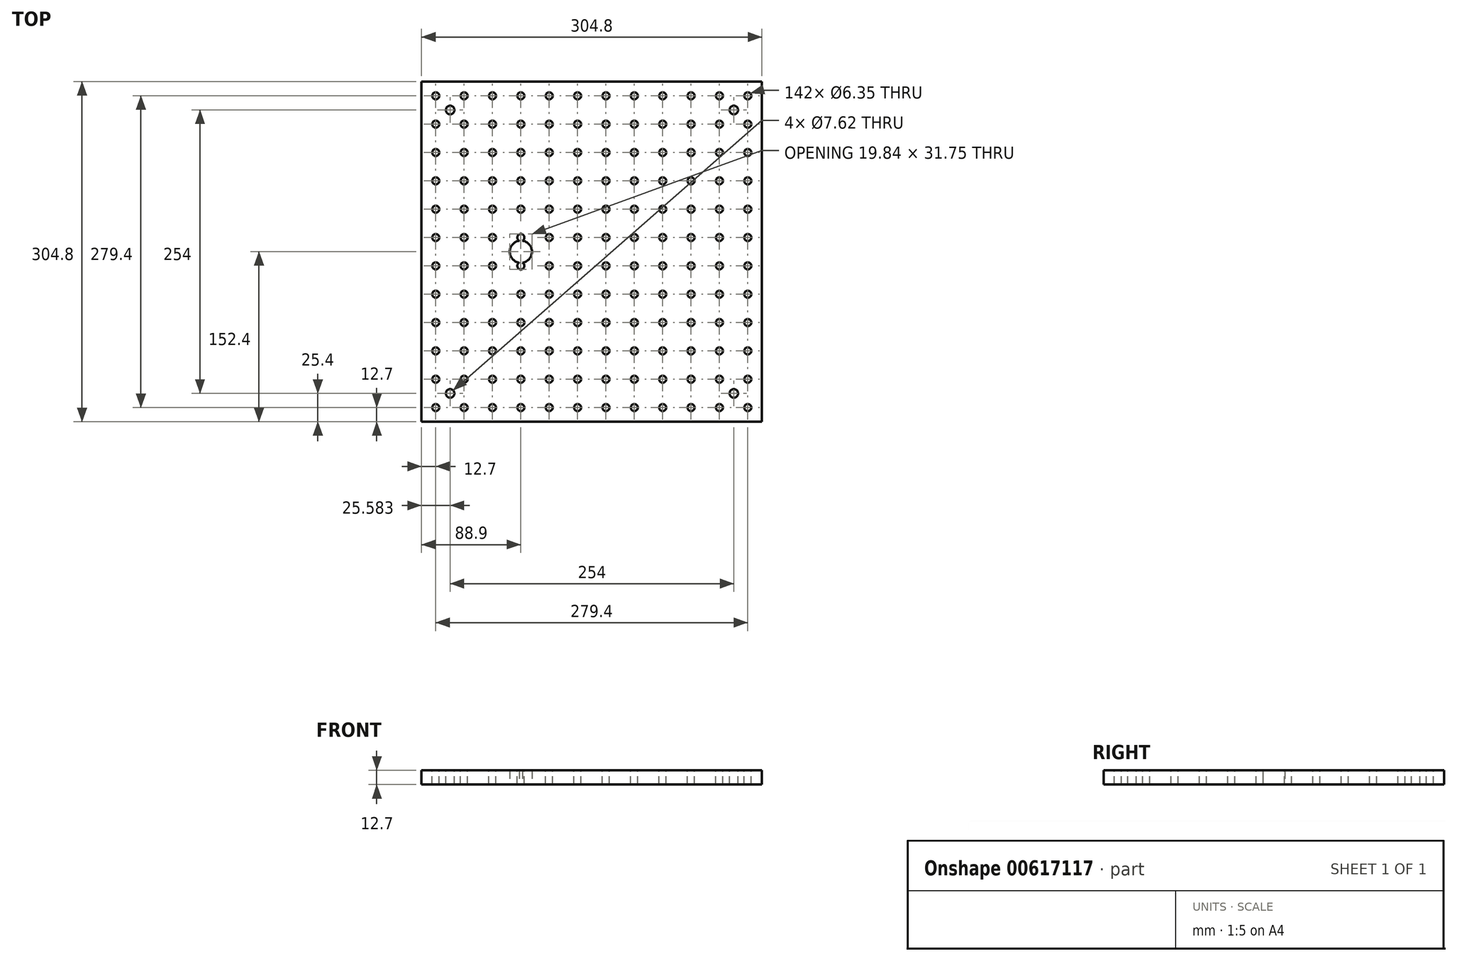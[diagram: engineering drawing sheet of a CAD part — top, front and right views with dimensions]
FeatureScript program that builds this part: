
annotation { "Feature Type Name" : "Feature", "Feature Type Description" : "" }
export const myFeature = defineFeature(function(context is Context, id is Id, definition is map)
    precondition{}
    {
        {
            var Q0;
            Q0=qCreatedBy(makeId("Top.planeOp"),FACE);
            var sketch = newSketch(context, id + "F0", { "sketchPlane" : qUnion([Q0])});
            skLineSegment(sketch, "E0.bottom", {"start": v(-152.4, 152.4) * mm, "end": v(152.4, 152.4) * mm});
            skLineSegment(sketch, "E0.top", {"start": v(-152.4, -152.4) * mm, "end": v(152.4, -152.4) * mm});
            skLineSegment(sketch, "E0.left", {"start": v(-152.4, 152.4) * mm, "end": v(-152.4, -152.4) * mm});
            skLineSegment(sketch, "E0.right", {"start": v(152.4, 152.4) * mm, "end": v(152.4, -152.4) * mm});
            skSolve(sketch);
        }
        {
            var Q0;
            Q0=qSketchRegion(id+"F0",true);
            extrude(context, id + "F1", {"entities" : qUnion([Q0]), "depth" : 12.7 * mm, "offsetDistance" : 25.4 * mm});
        }
        {
            var Q0;
            Q0=makeQuery(id+"F1.opExtrude","CAP_FACE",FACE,{"disambiguationData":[OSD([sQuery(id+"F0.wireOp",EDGE,"E0.bottom"),sQuery(id+"F0.wireOp",EDGE,"E0.top"),sQuery(id+"F0.wireOp",EDGE,"E0.left"),sQuery(id+"F0.wireOp",EDGE,"E0.right")])],"isStart":false});
            var sketch = newSketch(context, id + "F2", { "sketchPlane" : qUnion([Q0])});
            skCircle(sketch, "E1", {"center": v(-139.7, -139.7) * mm, "radius": 3.18 * mm});
            skCircle(sketch, "E2.0.1.0", {"center": v(-139.7, -114.3) * mm, "radius": 3.18 * mm});
            skCircle(sketch, "E2.0.2.0", {"center": v(-139.7, -88.9) * mm, "radius": 3.18 * mm});
            skCircle(sketch, "E2.0.3.0", {"center": v(-139.7, -63.5) * mm, "radius": 3.18 * mm});
            skCircle(sketch, "E2.0.4.0", {"center": v(-139.7, -38.1) * mm, "radius": 3.18 * mm});
            skCircle(sketch, "E2.0.5.0", {"center": v(-139.7, -12.7) * mm, "radius": 3.18 * mm});
            skCircle(sketch, "E2.0.6.0", {"center": v(-139.7, 12.7) * mm, "radius": 3.18 * mm});
            skCircle(sketch, "E2.0.7.0", {"center": v(-139.7, 38.1) * mm, "radius": 3.18 * mm});
            skCircle(sketch, "E2.0.8.0", {"center": v(-139.7, 63.5) * mm, "radius": 3.18 * mm});
            skCircle(sketch, "E2.0.9.0", {"center": v(-139.7, 88.9) * mm, "radius": 3.18 * mm});
            skCircle(sketch, "E2.0.10.0", {"center": v(-139.7, 114.3) * mm, "radius": 3.18 * mm});
            skCircle(sketch, "E2.1.0.0", {"center": v(-114.3, -139.7) * mm, "radius": 3.18 * mm});
            skCircle(sketch, "E2.1.1.0", {"center": v(-114.3, -114.3) * mm, "radius": 3.18 * mm});
            skCircle(sketch, "E2.1.2.0", {"center": v(-114.3, -88.9) * mm, "radius": 3.18 * mm});
            skCircle(sketch, "E2.1.3.0", {"center": v(-114.3, -63.5) * mm, "radius": 3.18 * mm});
            skCircle(sketch, "E2.1.4.0", {"center": v(-114.3, -38.1) * mm, "radius": 3.18 * mm});
            skCircle(sketch, "E2.1.5.0", {"center": v(-114.3, -12.7) * mm, "radius": 3.18 * mm});
            skCircle(sketch, "E2.1.6.0", {"center": v(-114.3, 12.7) * mm, "radius": 3.18 * mm});
            skCircle(sketch, "E2.1.7.0", {"center": v(-114.3, 38.1) * mm, "radius": 3.18 * mm});
            skCircle(sketch, "E2.1.8.0", {"center": v(-114.3, 63.5) * mm, "radius": 3.18 * mm});
            skCircle(sketch, "E2.1.9.0", {"center": v(-114.3, 88.9) * mm, "radius": 3.18 * mm});
            skCircle(sketch, "E2.1.10.0", {"center": v(-114.3, 114.3) * mm, "radius": 3.18 * mm});
            skCircle(sketch, "E2.2.0.0", {"center": v(-88.9, -139.7) * mm, "radius": 3.18 * mm});
            skCircle(sketch, "E2.2.1.0", {"center": v(-88.9, -114.3) * mm, "radius": 3.18 * mm});
            skCircle(sketch, "E2.2.2.0", {"center": v(-88.9, -88.9) * mm, "radius": 3.18 * mm});
            skCircle(sketch, "E2.2.3.0", {"center": v(-88.9, -63.5) * mm, "radius": 3.18 * mm});
            skCircle(sketch, "E2.2.4.0", {"center": v(-88.9, -38.1) * mm, "radius": 3.18 * mm});
            skCircle(sketch, "E2.2.5.0", {"center": v(-88.9, -12.7) * mm, "radius": 3.18 * mm});
            skCircle(sketch, "E2.2.6.0", {"center": v(-88.9, 12.7) * mm, "radius": 3.18 * mm});
            skCircle(sketch, "E2.2.7.0", {"center": v(-88.9, 38.1) * mm, "radius": 3.18 * mm});
            skCircle(sketch, "E2.2.8.0", {"center": v(-88.9, 63.5) * mm, "radius": 3.18 * mm});
            skCircle(sketch, "E2.2.9.0", {"center": v(-88.9, 88.9) * mm, "radius": 3.18 * mm});
            skCircle(sketch, "E2.2.10.0", {"center": v(-88.9, 114.3) * mm, "radius": 3.18 * mm});
            skCircle(sketch, "E2.3.0.0", {"center": v(-63.5, -139.7) * mm, "radius": 3.18 * mm});
            skCircle(sketch, "E2.3.1.0", {"center": v(-63.5, -114.3) * mm, "radius": 3.18 * mm});
            skCircle(sketch, "E2.3.2.0", {"center": v(-63.5, -88.9) * mm, "radius": 3.18 * mm});
            skCircle(sketch, "E2.3.3.0", {"center": v(-63.5, -63.5) * mm, "radius": 3.18 * mm});
            skCircle(sketch, "E2.3.4.0", {"center": v(-63.5, -38.1) * mm, "radius": 3.18 * mm});
            skCircle(sketch, "E2.3.5.0", {"center": v(-63.5, -12.7) * mm, "radius": 3.18 * mm});
            skCircle(sketch, "E2.3.6.0", {"center": v(-63.5, 12.7) * mm, "radius": 3.18 * mm});
            skCircle(sketch, "E2.3.7.0", {"center": v(-63.5, 38.1) * mm, "radius": 3.18 * mm});
            skCircle(sketch, "E2.3.8.0", {"center": v(-63.5, 63.5) * mm, "radius": 3.18 * mm});
            skCircle(sketch, "E2.3.9.0", {"center": v(-63.5, 88.9) * mm, "radius": 3.18 * mm});
            skCircle(sketch, "E2.3.10.0", {"center": v(-63.5, 114.3) * mm, "radius": 3.18 * mm});
            skCircle(sketch, "E2.4.0.0", {"center": v(-38.1, -139.7) * mm, "radius": 3.18 * mm});
            skCircle(sketch, "E2.4.1.0", {"center": v(-38.1, -114.3) * mm, "radius": 3.18 * mm});
            skCircle(sketch, "E2.4.2.0", {"center": v(-38.1, -88.9) * mm, "radius": 3.18 * mm});
            skCircle(sketch, "E2.4.3.0", {"center": v(-38.1, -63.5) * mm, "radius": 3.18 * mm});
            skCircle(sketch, "E2.4.4.0", {"center": v(-38.1, -38.1) * mm, "radius": 3.18 * mm});
            skCircle(sketch, "E2.4.5.0", {"center": v(-38.1, -12.7) * mm, "radius": 3.18 * mm});
            skCircle(sketch, "E2.4.6.0", {"center": v(-38.1, 12.7) * mm, "radius": 3.18 * mm});
            skCircle(sketch, "E2.4.7.0", {"center": v(-38.1, 38.1) * mm, "radius": 3.18 * mm});
            skCircle(sketch, "E2.4.8.0", {"center": v(-38.1, 63.5) * mm, "radius": 3.18 * mm});
            skCircle(sketch, "E2.4.9.0", {"center": v(-38.1, 88.9) * mm, "radius": 3.18 * mm});
            skCircle(sketch, "E2.4.10.0", {"center": v(-38.1, 114.3) * mm, "radius": 3.18 * mm});
            skCircle(sketch, "E2.5.0.0", {"center": v(-12.7, -139.7) * mm, "radius": 3.18 * mm});
            skCircle(sketch, "E2.5.1.0", {"center": v(-12.7, -114.3) * mm, "radius": 3.18 * mm});
            skCircle(sketch, "E2.5.2.0", {"center": v(-12.7, -88.9) * mm, "radius": 3.18 * mm});
            skCircle(sketch, "E2.5.3.0", {"center": v(-12.7, -63.5) * mm, "radius": 3.18 * mm});
            skCircle(sketch, "E2.5.4.0", {"center": v(-12.7, -38.1) * mm, "radius": 3.18 * mm});
            skCircle(sketch, "E2.5.5.0", {"center": v(-12.7, -12.7) * mm, "radius": 3.18 * mm});
            skCircle(sketch, "E2.5.6.0", {"center": v(-12.7, 12.7) * mm, "radius": 3.18 * mm});
            skCircle(sketch, "E2.5.7.0", {"center": v(-12.7, 38.1) * mm, "radius": 3.18 * mm});
            skCircle(sketch, "E2.5.8.0", {"center": v(-12.7, 63.5) * mm, "radius": 3.18 * mm});
            skCircle(sketch, "E2.5.9.0", {"center": v(-12.7, 88.9) * mm, "radius": 3.18 * mm});
            skCircle(sketch, "E2.5.10.0", {"center": v(-12.7, 114.3) * mm, "radius": 3.18 * mm});
            skCircle(sketch, "E2.6.0.0", {"center": v(12.7, -139.7) * mm, "radius": 3.18 * mm});
            skCircle(sketch, "E2.6.1.0", {"center": v(12.7, -114.3) * mm, "radius": 3.18 * mm});
            skCircle(sketch, "E2.6.2.0", {"center": v(12.7, -88.9) * mm, "radius": 3.18 * mm});
            skCircle(sketch, "E2.6.3.0", {"center": v(12.7, -63.5) * mm, "radius": 3.18 * mm});
            skCircle(sketch, "E2.6.4.0", {"center": v(12.7, -38.1) * mm, "radius": 3.18 * mm});
            skCircle(sketch, "E2.6.5.0", {"center": v(12.7, -12.7) * mm, "radius": 3.18 * mm});
            skCircle(sketch, "E2.6.6.0", {"center": v(12.7, 12.7) * mm, "radius": 3.18 * mm});
            skCircle(sketch, "E2.6.7.0", {"center": v(12.7, 38.1) * mm, "radius": 3.18 * mm});
            skCircle(sketch, "E2.6.8.0", {"center": v(12.7, 63.5) * mm, "radius": 3.18 * mm});
            skCircle(sketch, "E2.6.9.0", {"center": v(12.7, 88.9) * mm, "radius": 3.18 * mm});
            skCircle(sketch, "E2.6.10.0", {"center": v(12.7, 114.3) * mm, "radius": 3.18 * mm});
            skCircle(sketch, "E2.7.0.0", {"center": v(38.1, -139.7) * mm, "radius": 3.18 * mm});
            skCircle(sketch, "E2.7.1.0", {"center": v(38.1, -114.3) * mm, "radius": 3.18 * mm});
            skCircle(sketch, "E2.7.2.0", {"center": v(38.1, -88.9) * mm, "radius": 3.18 * mm});
            skCircle(sketch, "E2.7.3.0", {"center": v(38.1, -63.5) * mm, "radius": 3.18 * mm});
            skCircle(sketch, "E2.7.4.0", {"center": v(38.1, -38.1) * mm, "radius": 3.18 * mm});
            skCircle(sketch, "E2.7.5.0", {"center": v(38.1, -12.7) * mm, "radius": 3.18 * mm});
            skCircle(sketch, "E2.7.6.0", {"center": v(38.1, 12.7) * mm, "radius": 3.18 * mm});
            skCircle(sketch, "E2.7.7.0", {"center": v(38.1, 38.1) * mm, "radius": 3.18 * mm});
            skCircle(sketch, "E2.7.8.0", {"center": v(38.1, 63.5) * mm, "radius": 3.18 * mm});
            skCircle(sketch, "E2.7.9.0", {"center": v(38.1, 88.9) * mm, "radius": 3.18 * mm});
            skCircle(sketch, "E2.7.10.0", {"center": v(38.1, 114.3) * mm, "radius": 3.18 * mm});
            skCircle(sketch, "E2.8.0.0", {"center": v(63.5, -139.7) * mm, "radius": 3.18 * mm});
            skCircle(sketch, "E2.8.1.0", {"center": v(63.5, -114.3) * mm, "radius": 3.18 * mm});
            skCircle(sketch, "E2.8.2.0", {"center": v(63.5, -88.9) * mm, "radius": 3.18 * mm});
            skCircle(sketch, "E2.8.3.0", {"center": v(63.5, -63.5) * mm, "radius": 3.18 * mm});
            skCircle(sketch, "E2.8.4.0", {"center": v(63.5, -38.1) * mm, "radius": 3.18 * mm});
            skCircle(sketch, "E2.8.5.0", {"center": v(63.5, -12.7) * mm, "radius": 3.18 * mm});
            skCircle(sketch, "E2.8.6.0", {"center": v(63.5, 12.7) * mm, "radius": 3.18 * mm});
            skCircle(sketch, "E2.8.7.0", {"center": v(63.5, 38.1) * mm, "radius": 3.18 * mm});
            skCircle(sketch, "E2.8.8.0", {"center": v(63.5, 63.5) * mm, "radius": 3.18 * mm});
            skCircle(sketch, "E2.8.9.0", {"center": v(63.5, 88.9) * mm, "radius": 3.18 * mm});
            skCircle(sketch, "E2.8.10.0", {"center": v(63.5, 114.3) * mm, "radius": 3.18 * mm});
            skCircle(sketch, "E2.9.0.0", {"center": v(88.9, -139.7) * mm, "radius": 3.18 * mm});
            skCircle(sketch, "E2.9.1.0", {"center": v(88.9, -114.3) * mm, "radius": 3.18 * mm});
            skCircle(sketch, "E2.9.2.0", {"center": v(88.9, -88.9) * mm, "radius": 3.18 * mm});
            skCircle(sketch, "E2.9.3.0", {"center": v(88.9, -63.5) * mm, "radius": 3.18 * mm});
            skCircle(sketch, "E2.9.4.0", {"center": v(88.9, -38.1) * mm, "radius": 3.18 * mm});
            skCircle(sketch, "E2.9.5.0", {"center": v(88.9, -12.7) * mm, "radius": 3.18 * mm});
            skCircle(sketch, "E2.9.6.0", {"center": v(88.9, 12.7) * mm, "radius": 3.18 * mm});
            skCircle(sketch, "E2.9.7.0", {"center": v(88.9, 38.1) * mm, "radius": 3.18 * mm});
            skCircle(sketch, "E2.9.8.0", {"center": v(88.9, 63.5) * mm, "radius": 3.18 * mm});
            skCircle(sketch, "E2.9.9.0", {"center": v(88.9, 88.9) * mm, "radius": 3.18 * mm});
            skCircle(sketch, "E2.9.10.0", {"center": v(88.9, 114.3) * mm, "radius": 3.18 * mm});
            skCircle(sketch, "E2.10.0.0", {"center": v(114.3, -139.7) * mm, "radius": 3.18 * mm});
            skCircle(sketch, "E2.10.1.0", {"center": v(114.3, -114.3) * mm, "radius": 3.18 * mm});
            skCircle(sketch, "E2.10.2.0", {"center": v(114.3, -88.9) * mm, "radius": 3.18 * mm});
            skCircle(sketch, "E2.10.3.0", {"center": v(114.3, -63.5) * mm, "radius": 3.18 * mm});
            skCircle(sketch, "E2.10.4.0", {"center": v(114.3, -38.1) * mm, "radius": 3.18 * mm});
            skCircle(sketch, "E2.10.5.0", {"center": v(114.3, -12.7) * mm, "radius": 3.18 * mm});
            skCircle(sketch, "E2.10.6.0", {"center": v(114.3, 12.7) * mm, "radius": 3.18 * mm});
            skCircle(sketch, "E2.10.7.0", {"center": v(114.3, 38.1) * mm, "radius": 3.18 * mm});
            skCircle(sketch, "E2.10.8.0", {"center": v(114.3, 63.5) * mm, "radius": 3.18 * mm});
            skCircle(sketch, "E2.10.9.0", {"center": v(114.3, 88.9) * mm, "radius": 3.18 * mm});
            skCircle(sketch, "E2.10.10.0", {"center": v(114.3, 114.3) * mm, "radius": 3.18 * mm});
            skLineSegment(sketch, "E2.direction1", {"start": v(-139.7, -139.7) * mm, "end": v(-114.3, -139.7) * mm, "construction": true});
            skLineSegment(sketch, "E2.direction2", {"start": v(-139.7, -139.7) * mm, "end": v(-139.7, -114.3) * mm, "construction": true});
            skCircle(sketch, "E3.0.11.0", {"center": v(139.7, -139.7) * mm, "radius": 3.18 * mm});
            skCircle(sketch, "E3.0.11.1", {"center": v(139.7, -114.3) * mm, "radius": 3.18 * mm});
            skCircle(sketch, "E3.0.11.2", {"center": v(139.7, -88.9) * mm, "radius": 3.18 * mm});
            skCircle(sketch, "E3.0.11.3", {"center": v(139.7, -63.5) * mm, "radius": 3.18 * mm});
            skCircle(sketch, "E3.0.11.4", {"center": v(139.7, -38.1) * mm, "radius": 3.18 * mm});
            skCircle(sketch, "E3.0.11.5", {"center": v(139.7, -12.7) * mm, "radius": 3.18 * mm});
            skCircle(sketch, "E3.0.11.6", {"center": v(139.7, 12.7) * mm, "radius": 3.18 * mm});
            skCircle(sketch, "E3.0.11.7", {"center": v(139.7, 38.1) * mm, "radius": 3.18 * mm});
            skCircle(sketch, "E3.0.11.8", {"center": v(139.7, 63.5) * mm, "radius": 3.18 * mm});
            skCircle(sketch, "E3.0.11.9", {"center": v(139.7, 88.9) * mm, "radius": 3.18 * mm});
            skCircle(sketch, "E3.0.11.10", {"center": v(139.7, 114.3) * mm, "radius": 3.18 * mm});
            skCircle(sketch, "E4.0.0.11", {"center": v(-139.7, 139.7) * mm, "radius": 3.18 * mm});
            skCircle(sketch, "E4.0.1.11", {"center": v(-114.3, 139.7) * mm, "radius": 3.18 * mm});
            skCircle(sketch, "E4.0.2.11", {"center": v(-88.9, 139.7) * mm, "radius": 3.18 * mm});
            skCircle(sketch, "E4.0.3.11", {"center": v(-63.5, 139.7) * mm, "radius": 3.18 * mm});
            skCircle(sketch, "E4.0.4.11", {"center": v(-38.1, 139.7) * mm, "radius": 3.18 * mm});
            skCircle(sketch, "E4.0.5.11", {"center": v(-12.7, 139.7) * mm, "radius": 3.18 * mm});
            skCircle(sketch, "E4.0.6.11", {"center": v(12.7, 139.7) * mm, "radius": 3.18 * mm});
            skCircle(sketch, "E4.0.7.11", {"center": v(38.1, 139.7) * mm, "radius": 3.18 * mm});
            skCircle(sketch, "E4.0.8.11", {"center": v(63.5, 139.7) * mm, "radius": 3.18 * mm});
            skCircle(sketch, "E4.0.9.11", {"center": v(88.9, 139.7) * mm, "radius": 3.18 * mm});
            skCircle(sketch, "E4.0.10.11", {"center": v(114.3, 139.7) * mm, "radius": 3.18 * mm});
            skCircle(sketch, "E4.0.11.11", {"center": v(139.7, 139.7) * mm, "radius": 3.18 * mm});
            skCircle(sketch, "E5", {"center": v(-126.82, -127) * mm, "radius": 3.81 * mm});
            skCircle(sketch, "E6.0.1.0", {"center": v(-126.82, 127) * mm, "radius": 3.81 * mm});
            skCircle(sketch, "E6.1.0.0", {"center": v(127.18, -127) * mm, "radius": 3.81 * mm});
            skCircle(sketch, "E6.1.1.0", {"center": v(127.18, 127) * mm, "radius": 3.81 * mm});
            skCircle(sketch, "E6.2.0.0", {"center": v(381.18, -127) * mm, "radius": 3.81 * mm});
            skCircle(sketch, "E6.2.1.0", {"center": v(381.18, 127) * mm, "radius": 3.81 * mm});
            skLineSegment(sketch, "E6.direction1", {"start": v(-126.82, -127) * mm, "end": v(127.18, -127) * mm, "construction": true});
            skLineSegment(sketch, "E6.direction2", {"start": v(-126.82, -127) * mm, "end": v(-126.82, 127) * mm, "construction": true});
            skSolve(sketch);
        }
        {
            var Q0;
            Q0=qSketchRegion(id+"F2",true);
            extrude(context, id + "F3", {"entities" : qUnion([Q0]), "operationType" : NewBodyOperationType.REMOVE, "oppositeDirection" : true, "depth" : 25.4 * mm, "offsetDistance" : 25.4 * mm});
        }
        {
            var Q0;
            Q0=qCreatedBy(makeId("Top.planeOp"),FACE);
            var sketch = newSketch(context, id + "F4", { "sketchPlane" : qUnion([Q0])});
            skCircle(sketch, "E7", {"center": v(-63.5, 0) * mm, "radius": 9.92 * mm});
            skSolve(sketch);
        }
        {
            var Q0;
            Q0=qSketchRegion(id+"F4",true);
            extrude(context, id + "F5", {"entities" : qUnion([Q0]), "operationType" : NewBodyOperationType.REMOVE, "depth" : 25.4 * mm, "offsetDistance" : 25.4 * mm});
        }
    });
